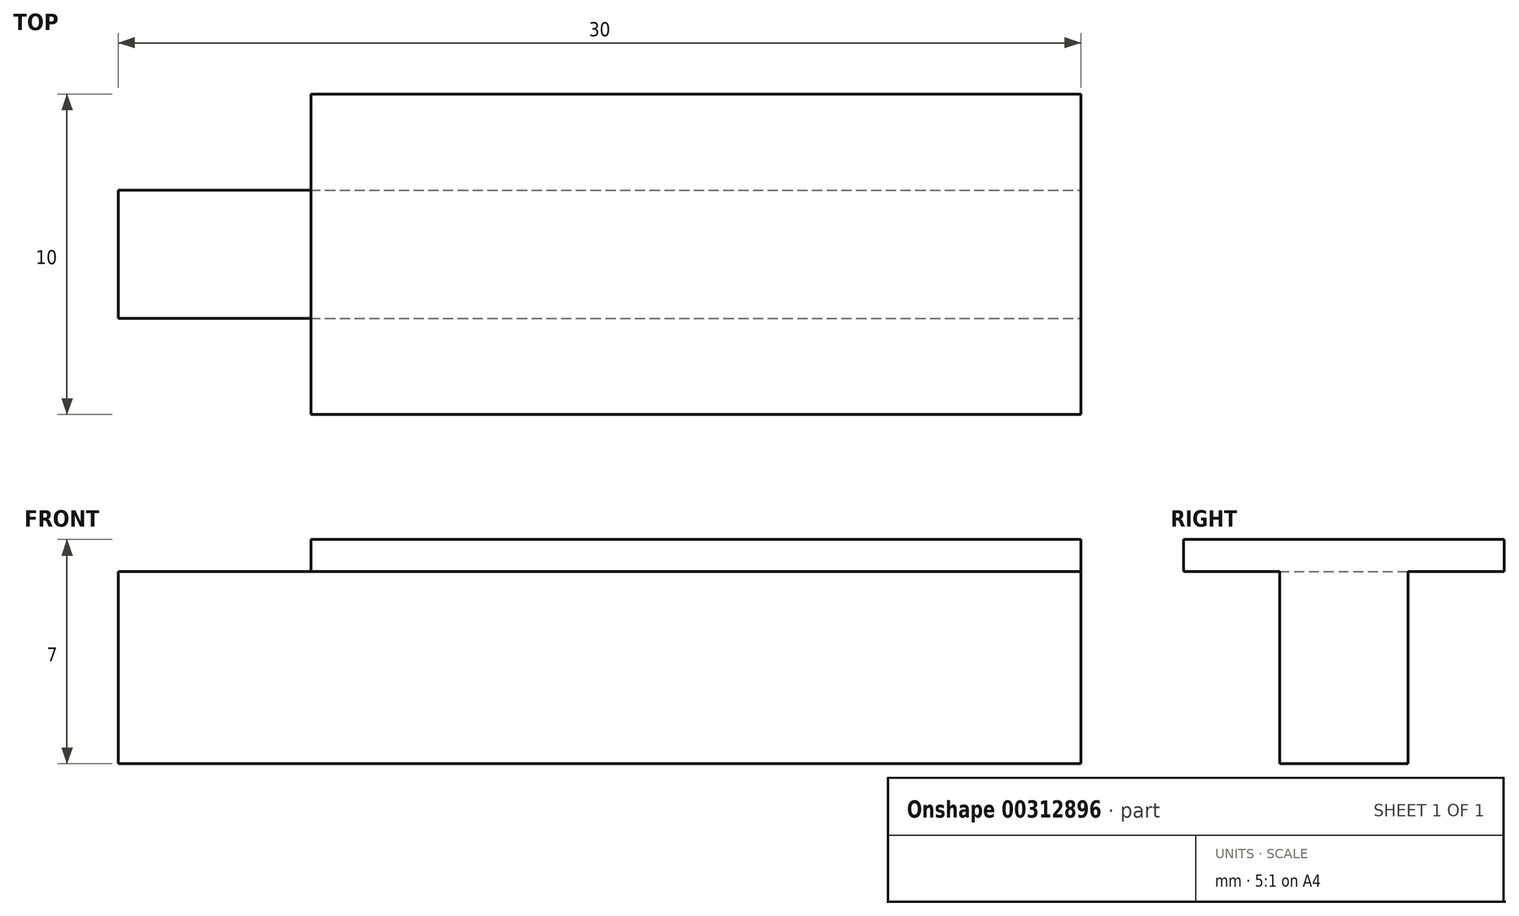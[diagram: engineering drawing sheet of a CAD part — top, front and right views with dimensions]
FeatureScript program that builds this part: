
annotation { "Feature Type Name" : "Feature", "Feature Type Description" : "" }
export const myFeature = defineFeature(function(context is Context, id is Id, definition is map)
    precondition{}
    {
        {
            var Q0;
            Q0=qCreatedBy(makeId("Top.planeOp"),FACE);
            var sketch = newSketch(context, id + "F0", { "sketchPlane" : qUnion([Q0])});
            skLineSegment(sketch, "E0.bottom", {"start": v(0, 0) * mm, "end": v(30, 0) * mm});
            skLineSegment(sketch, "E0.top", {"start": v(0, 4) * mm, "end": v(30, 4) * mm});
            skLineSegment(sketch, "E0.left", {"start": v(0, 0) * mm, "end": v(0, 4) * mm});
            skLineSegment(sketch, "E0.right", {"start": v(30, 0) * mm, "end": v(30, 4) * mm});
            skSolve(sketch);
        }
        {
            var Q0;
            Q0 = qSketchRegion(id + "F0", true);
            extrude(context, id + "F1", {"entities" : qUnion([Q0]), "oppositeDirection" : true, "depth" : 6 * mm, "offsetDistance" : 25 * mm});
        }
        {
            var Q0;
            Q0=makeQuery(id+"F1.opExtrude","CAP_FACE",FACE,{"disambiguationData":[OSD([sQuery(id+"F0.wireOp",EDGE,"E0.bottom"),sQuery(id+"F0.wireOp",EDGE,"E0.top"),sQuery(id+"F0.wireOp",EDGE,"E0.left"),sQuery(id+"F0.wireOp",EDGE,"E0.right")])],"isStart":true});
            var sketch = newSketch(context, id + "F2", { "sketchPlane" : qUnion([Q0])});
            skLineSegment(sketch, "E1.bottom", {"start": v(6, 7) * mm, "end": v(30, 7) * mm});
            skLineSegment(sketch, "E1.top", {"start": v(6, -3) * mm, "end": v(30, -3) * mm});
            skLineSegment(sketch, "E1.left", {"start": v(6, 7) * mm, "end": v(6, -3) * mm});
            skLineSegment(sketch, "E1.right", {"start": v(30, 7) * mm, "end": v(30, -3) * mm});
            skSolve(sketch);
        }
        {
            var Q0;
            Q0 = qSketchRegion(id + "F2", true);
            extrude(context, id + "F3", {"entities" : qUnion([Q0]), "operationType" : NewBodyOperationType.ADD, "depth" : 1 * mm, "offsetDistance" : 25 * mm});
        }
    });
